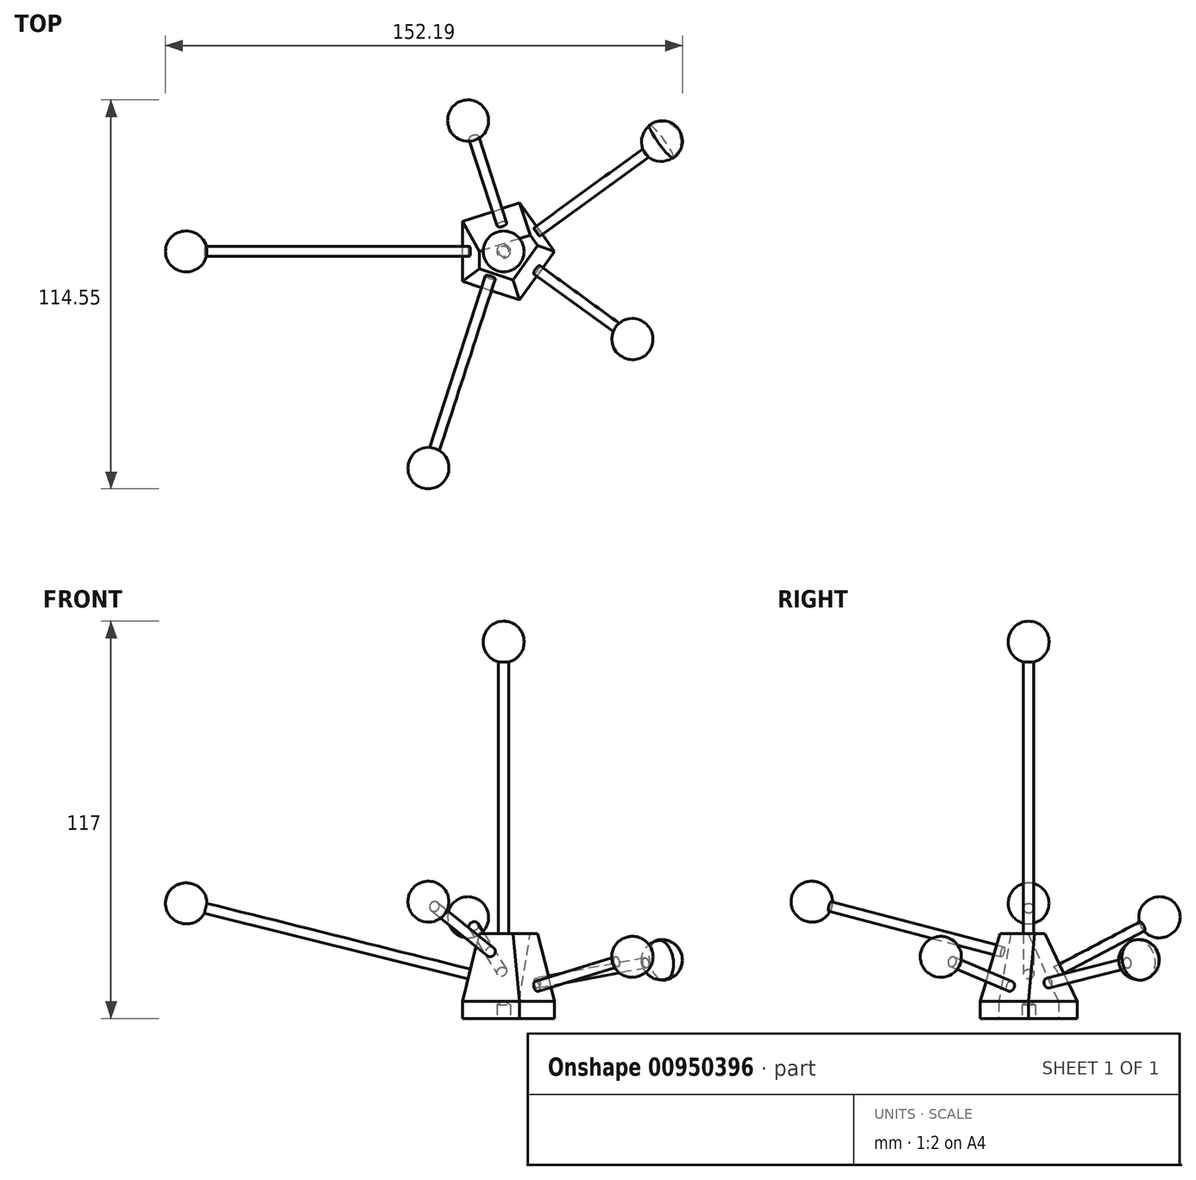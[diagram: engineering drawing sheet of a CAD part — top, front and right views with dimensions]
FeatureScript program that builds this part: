
annotation { "Feature Type Name" : "Feature", "Feature Type Description" : "" }
export const myFeature = defineFeature(function(context is Context, id is Id, definition is map)
    precondition{}
    {
        {
            var Q0;
            Q0=qCreatedBy(makeId("Top.planeOp"),FACE);
            var sketch = newSketch(context, id + "F0", { "sketchPlane" : qUnion([Q0])});
            skCircle(sketch, "E0.cCircle", {"center": v(0, 0) * mm, "radius": 12.14 * mm, "construction": true});
            skLineSegment(sketch, "E0.0", {"start": v(4.64, 14.27) * mm, "end": v(15, 0) * mm});
            skLineSegment(sketch, "E0.1", {"start": v(15, 0) * mm, "end": v(4.64, -14.27) * mm});
            skLineSegment(sketch, "E0.2", {"start": v(4.64, -14.27) * mm, "end": v(-12.14, -8.82) * mm});
            skLineSegment(sketch, "E0.3", {"start": v(-12.14, -8.82) * mm, "end": v(-12.14, 8.82) * mm});
            skLineSegment(sketch, "E0.4", {"start": v(-12.14, 8.82) * mm, "end": v(4.64, 14.27) * mm});
            skPoint(sketch, "E0.0.midPoint", {"position": v(9.82, 7.13) * mm});
            skSolve(sketch);
        }
        {
            var Q0;
            Q0 = qSketchRegion(id + "F0", true);
            extrude(context, id + "F1", {"entities" : qUnion([Q0]), "depth" : 25 * mm, "offsetDistance" : 25 * mm});
        }
        {
            var Q0;
            Q0=makeQuery(id+"F1.opExtrude","CAP_EDGE",EDGE,{"disambiguationData":[OSD([sQuery(id+"F0.wireOp",EDGE,"E0.2")])],"isStart":false});
            chamfer(context, id + "F2", {"entities" : qUnion([Q0]), "chamferType" : ChamferType.TWO_OFFSETS, "width1" : 20 * mm, "oppositeDirection" : false, "width2" : 5 * mm, "tangentPropagation" : true});
        }
        {
            var Q0;
            Q0=makeQuery(id+"F1.opExtrude","CAP_EDGE",EDGE,{"disambiguationData":[OSD([sQuery(id+"F0.wireOp",EDGE,"E0.1")])],"isStart":false});
            chamfer(context, id + "F3", {"entities" : qUnion([Q0]), "chamferType" : ChamferType.TWO_OFFSETS, "width1" : 20 * mm, "oppositeDirection" : false, "width2" : 5 * mm, "tangentPropagation" : true});
        }
        {
            var Q0;
            Q0=makeQuery(id+"F1.opExtrude","CAP_EDGE",EDGE,{"disambiguationData":[OSD([sQuery(id+"F0.wireOp",EDGE,"E0.0")])],"isStart":false});
            chamfer(context, id + "F4", {"entities" : qUnion([Q0]), "chamferType" : ChamferType.TWO_OFFSETS, "width1" : 20 * mm, "oppositeDirection" : false, "width2" : 3 * mm, "tangentPropagation" : true});
        }
        {
            var Q0;
            Q0=makeQuery(id+"F1.opExtrude","CAP_EDGE",EDGE,{"disambiguationData":[OSD([sQuery(id+"F0.wireOp",EDGE,"E0.4")])],"isStart":false});
            chamfer(context, id + "F5", {"entities" : qUnion([Q0]), "chamferType" : ChamferType.TWO_OFFSETS, "width1" : 20 * mm, "oppositeDirection" : false, "width2" : 10 * mm, "tangentPropagation" : true});
        }
        {
            var Q0;
            Q0=makeQuery(id+"F1.opExtrude","CAP_EDGE",EDGE,{"disambiguationData":[OSD([sQuery(id+"F0.wireOp",EDGE,"E0.3")])],"isStart":false});
            chamfer(context, id + "F6", {"entities" : qUnion([Q0]), "chamferType" : ChamferType.TWO_OFFSETS, "width1" : 20 * mm, "oppositeDirection" : false, "width2" : 5 * mm, "tangentPropagation" : true});
        }
        {
            var Q0;
            Q0=makeQuery(id+"F6.opChamfer","BLEND_FACE",FACE,{"disambiguationData":[OSD([sQuery(id+"F0.wireOp",EDGE,"E0.3")])]});
            var sketch = newSketch(context, id + "F7", { "sketchPlane" : qUnion([Q0])});
            skCircle(sketch, "E1", {"center": v(0, 10.2) * mm, "radius": 1.5 * mm});
            skSolve(sketch);
        }
        {
            var Q0;
            Q0=makeQuery(id+"F5.opChamfer","BLEND_FACE",FACE,{"disambiguationData":[OSD([sQuery(id+"F0.wireOp",EDGE,"E0.4")])]});
            var sketch = newSketch(context, id + "F8", { "sketchPlane" : qUnion([Q0])});
            skCircle(sketch, "E2", {"center": v(-3.2, 8.44) * mm, "radius": 1.5 * mm});
            skSolve(sketch);
        }
        {
            var Q0;
            Q0=makeQuery(id+"F4.opChamfer","BLEND_FACE",FACE,{"disambiguationData":[OSD([sQuery(id+"F0.wireOp",EDGE,"E0.0")])]});
            var sketch = newSketch(context, id + "F9", { "sketchPlane" : qUnion([Q0])});
            skCircle(sketch, "E3", {"center": v(-2.04, 8.44) * mm, "radius": 1.5 * mm});
            skSolve(sketch);
        }
        {
            var Q0;
            Q0=makeQuery(id+"F3.opChamfer","BLEND_FACE",FACE,{"disambiguationData":[OSD([sQuery(id+"F0.wireOp",EDGE,"E0.1")])]});
            var sketch = newSketch(context, id + "F10", { "sketchPlane" : qUnion([Q0])});
            skCircle(sketch, "E4", {"center": v(2.46, 6.15) * mm, "radius": 1.5 * mm});
            skSolve(sketch);
        }
        {
            var Q0;
            Q0=makeQuery(id+"F1.opExtrude","CAP_FACE",FACE,{"disambiguationData":[OSD([sQuery(id+"F0.wireOp",EDGE,"E0.0"),sQuery(id+"F0.wireOp",EDGE,"E0.1"),sQuery(id+"F0.wireOp",EDGE,"E0.2"),sQuery(id+"F0.wireOp",EDGE,"E0.3"),sQuery(id+"F0.wireOp",EDGE,"E0.4")])],"isStart":false});
            var sketch = newSketch(context, id + "F11", { "sketchPlane" : qUnion([Q0])});
            skCircle(sketch, "E5", {"center": v(0, 0) * mm, "radius": 1.5 * mm});
            skSolve(sketch);
        }
        {
            var Q0;
            Q0=makeQuery(id+"F2.opChamfer","BLEND_FACE",FACE,{"disambiguationData":[OSD([sQuery(id+"F0.wireOp",EDGE,"E0.2")])]});
            var sketch = newSketch(context, id + "F12", { "sketchPlane" : qUnion([Q0])});
            skCircle(sketch, "E6", {"center": v(0, 17.03) * mm, "radius": 1.5 * mm});
            skSolve(sketch);
        }
        {
            var Q0;
            Q0 = qSketchRegion(id + "F7", true);
            extrude(context, id + "F13", {"entities" : qUnion([Q0]), "operationType" : NewBodyOperationType.ADD, "depth" : 80 * mm, "offsetDistance" : 25 * mm});
        }
        {
            var Q0;
            Q0 = qSketchRegion(id + "F8", true);
            extrude(context, id + "F14", {"entities" : qUnion([Q0]), "operationType" : NewBodyOperationType.ADD, "depth" : 30 * mm, "offsetDistance" : 25 * mm});
        }
        {
            var Q0;
            Q0 = qSketchRegion(id + "F9", true);
            extrude(context, id + "F15", {"entities" : qUnion([Q0]), "operationType" : NewBodyOperationType.ADD, "depth" : 40 * mm, "offsetDistance" : 25 * mm});
        }
        {
            var Q0;
            Q0 = qSketchRegion(id + "F10", true);
            extrude(context, id + "F16", {"entities" : qUnion([Q0]), "operationType" : NewBodyOperationType.ADD, "depth" : 30 * mm, "offsetDistance" : 25 * mm});
        }
        {
            var Q0;
            Q0 = qSketchRegion(id + "F11", true);
            extrude(context, id + "F17", {"entities" : qUnion([Q0]), "operationType" : NewBodyOperationType.ADD, "depth" : 80 * mm, "offsetDistance" : 25 * mm});
        }
        {
            var Q0;
            Q0 = qSketchRegion(id + "F12", true);
            extrude(context, id + "F18", {"entities" : qUnion([Q0]), "operationType" : NewBodyOperationType.ADD, "depth" : 55 * mm, "offsetDistance" : 25 * mm});
        }
        {
            var Q0;
            Q0=makeQuery(id+"F18.opExtrude","CAP_FACE",FACE,{"disambiguationData":[OSD([sQuery(id+"F12.wireOp",EDGE,"E6")])],"isStart":false});
            var sketch = newSketch(context, id + "F19", { "sketchPlane" : qUnion([Q0])});
            skCircle(sketch, "E7", {"center": v(0, 17.03) * mm, "radius": 6 * mm});
            skSolve(sketch);
        }
        {
            var Q0;
            Q0=makeQuery(id+"F16.opExtrude","CAP_FACE",FACE,{"disambiguationData":[OSD([sQuery(id+"F10.wireOp",EDGE,"E4")])],"isStart":false});
            var sketch = newSketch(context, id + "F20", { "sketchPlane" : qUnion([Q0])});
            skCircle(sketch, "E8", {"center": v(2.46, 6.15) * mm, "radius": 6 * mm});
            skSolve(sketch);
        }
        {
            var Q0;
            Q0=makeQuery(id+"F15.opExtrude","CAP_FACE",FACE,{"disambiguationData":[OSD([sQuery(id+"F9.wireOp",EDGE,"E3")])],"isStart":false});
            var sketch = newSketch(context, id + "F21", { "sketchPlane" : qUnion([Q0])});
            skCircle(sketch, "E9", {"center": v(-2.04, 8.44) * mm, "radius": 6 * mm});
            skSolve(sketch);
        }
        {
            var Q0;
            Q0=makeQuery(id+"F14.opExtrude","CAP_FACE",FACE,{"disambiguationData":[OSD([sQuery(id+"F8.wireOp",EDGE,"E2")])],"isStart":false});
            var sketch = newSketch(context, id + "F22", { "sketchPlane" : qUnion([Q0])});
            skCircle(sketch, "E10", {"center": v(-3.2, 8.44) * mm, "radius": 6 * mm});
            skSolve(sketch);
        }
        {
            var Q0;
            Q0=makeQuery(id+"F13.opExtrude","CAP_FACE",FACE,{"disambiguationData":[OSD([sQuery(id+"F7.wireOp",EDGE,"E1")])],"isStart":false});
            var sketch = newSketch(context, id + "F23", { "sketchPlane" : qUnion([Q0])});
            skCircle(sketch, "E11", {"center": v(0, 10.2) * mm, "radius": 6 * mm});
            skSolve(sketch);
        }
        {
            var Q0;
            Q0=makeQuery(id+"F17.opExtrude","CAP_FACE",FACE,{"disambiguationData":[OSD([sQuery(id+"F11.wireOp",EDGE,"E5")])],"isStart":false});
            var sketch = newSketch(context, id + "F24", { "sketchPlane" : qUnion([Q0])});
            skCircle(sketch, "E12", {"center": v(0, 0) * mm, "radius": 6 * mm});
            skSolve(sketch);
        }
        {
            var Q0;
            Q0 = qSketchRegion(id + "F19", true);
            extrude(context, id + "F25", {"entities" : qUnion([Q0]), "operationType" : NewBodyOperationType.ADD, "depth" : 12 * mm, "offsetDistance" : 25 * mm});
        }
        {
            var Q0;
            Q0 = qSketchRegion(id + "F20", true);
            extrude(context, id + "F26", {"entities" : qUnion([Q0]), "operationType" : NewBodyOperationType.ADD, "depth" : 12 * mm, "offsetDistance" : 25 * mm});
        }
        {
            var Q0;
            Q0 = qSketchRegion(id + "F21", true);
            extrude(context, id + "F27", {"entities" : qUnion([Q0]), "operationType" : NewBodyOperationType.ADD, "depth" : 12 * mm, "offsetDistance" : 25 * mm});
        }
        {
            var Q0;
            Q0 = qSketchRegion(id + "F22", true);
            extrude(context, id + "F28", {"entities" : qUnion([Q0]), "operationType" : NewBodyOperationType.ADD, "depth" : 12 * mm, "offsetDistance" : 25 * mm});
        }
        {
            var Q0;
            Q0 = qSketchRegion(id + "F23", true);
            extrude(context, id + "F29", {"entities" : qUnion([Q0]), "operationType" : NewBodyOperationType.ADD, "depth" : 12 * mm, "offsetDistance" : 25 * mm});
        }
        {
            var Q0;
            Q0 = qSketchRegion(id + "F24", true);
            extrude(context, id + "F30", {"entities" : qUnion([Q0]), "operationType" : NewBodyOperationType.ADD, "depth" : 12 * mm, "offsetDistance" : 25 * mm});
        }
        {
            var Q0;
            Q0=makeQuery(id+"F29.opExtrude","CAP_EDGE",EDGE,{"disambiguationData":[OSD([sQuery(id+"F23.wireOp",EDGE,"E11")])],"isStart":false});
            var Q1;
            Q1=makeQuery(id+"F28.opExtrude","CAP_EDGE",EDGE,{"disambiguationData":[OSD([sQuery(id+"F22.wireOp",EDGE,"E10")])],"isStart":false});
            var Q2;
            Q2=makeQuery(id+"F30.opExtrude","CAP_EDGE",EDGE,{"disambiguationData":[OSD([sQuery(id+"F24.wireOp",EDGE,"E12")])],"isStart":false});
            var Q3;
            Q3=makeQuery(id+"F27.opExtrude","CAP_EDGE",EDGE,{"disambiguationData":[OSD([sQuery(id+"F21.wireOp",EDGE,"E9")])],"isStart":false});
            var Q4;
            Q4=makeQuery(id+"F25.opExtrude","CAP_EDGE",EDGE,{"disambiguationData":[OSD([sQuery(id+"F19.wireOp",EDGE,"E7")])],"isStart":false});
            var Q5;
            Q5=makeQuery(id+"F26.opExtrude","CAP_EDGE",EDGE,{"disambiguationData":[OSD([sQuery(id+"F20.wireOp",EDGE,"E8")])],"isStart":false});
            fillet(context, id + "F31", {"entities" : qUnion([Q0, Q1, Q2, Q3, Q4, Q5]), "radius" : 6 * mm, "tangentPropagation" : true, "allowEdgeOverflow" : false});
        }
        {
            var Q0;
            Q0=makeQuery(id+"F28.opExtrude","CAP_EDGE",EDGE,{"disambiguationData":[OSD([sQuery(id+"F22.wireOp",EDGE,"E10")])],"isStart":true});
            var Q1;
            Q1=makeQuery(id+"F27.opExtrude","CAP_EDGE",EDGE,{"disambiguationData":[OSD([sQuery(id+"F21.wireOp",EDGE,"E9")])],"isStart":true});
            var Q2;
            Q2=makeQuery(id+"F30.opExtrude","CAP_EDGE",EDGE,{"disambiguationData":[OSD([sQuery(id+"F24.wireOp",EDGE,"E12")])],"isStart":true});
            var Q3;
            Q3=makeQuery(id+"F26.opExtrude","CAP_EDGE",EDGE,{"disambiguationData":[OSD([sQuery(id+"F20.wireOp",EDGE,"E8")])],"isStart":true});
            var Q4;
            Q4=makeQuery(id+"F25.opExtrude","CAP_EDGE",EDGE,{"disambiguationData":[OSD([sQuery(id+"F19.wireOp",EDGE,"E7")])],"isStart":true});
            var Q5;
            Q5=makeQuery(id+"F29.opExtrude","CAP_EDGE",EDGE,{"disambiguationData":[OSD([sQuery(id+"F23.wireOp",EDGE,"E11")])],"isStart":true});
            fillet(context, id + "F32", {"entities" : qUnion([Q0, Q1, Q2, Q3, Q4, Q5]), "radius" : 5.9 * mm, "tangentPropagation" : true, "allowEdgeOverflow" : false});
        }
        {
            var Q0;
            Q0=makeQuery(id+"F1.opExtrude","CAP_FACE",FACE,{"disambiguationData":[OSD([sQuery(id+"F0.wireOp",EDGE,"E0.0"),sQuery(id+"F0.wireOp",EDGE,"E0.1"),sQuery(id+"F0.wireOp",EDGE,"E0.2"),sQuery(id+"F0.wireOp",EDGE,"E0.3"),sQuery(id+"F0.wireOp",EDGE,"E0.4")])],"isStart":true});
            var sketch = newSketch(context, id + "F33", { "sketchPlane" : qUnion([Q0])});
            skPoint(sketch, "E13", {"position": v(0, 0) * mm});
            skSolve(sketch);
        }
        {
            var Q0;
            Q0=sQuery(id+"F33.wireOp",VERTEX,"E13");
            var Q1;
            Q1=makeQuery(id+"F1.opExtrude","SWEPT_BODY",BODY,{"disambiguationData":[OSD([sQuery(id+"F0.wireOp",EDGE,"E0.0"),sQuery(id+"F0.wireOp",EDGE,"E0.1"),sQuery(id+"F0.wireOp",EDGE,"E0.2"),sQuery(id+"F0.wireOp",EDGE,"E0.3"),sQuery(id+"F0.wireOp",EDGE,"E0.4")])]});
            hole(context, id + "F34", {"style" : HoleStyle.SIMPLE, "endStyle" : HoleEndStyle.BLIND, "holeDiameter" : 4 * mm, "majorDiameter" : 5 * mm, "holeDepth" : 4 * mm, "tappedDepth" : 12 * mm, "tapClearance" : 3, "locations" : qUnion([Q0]), "scope" : qUnion([Q1])});
        }
    });
